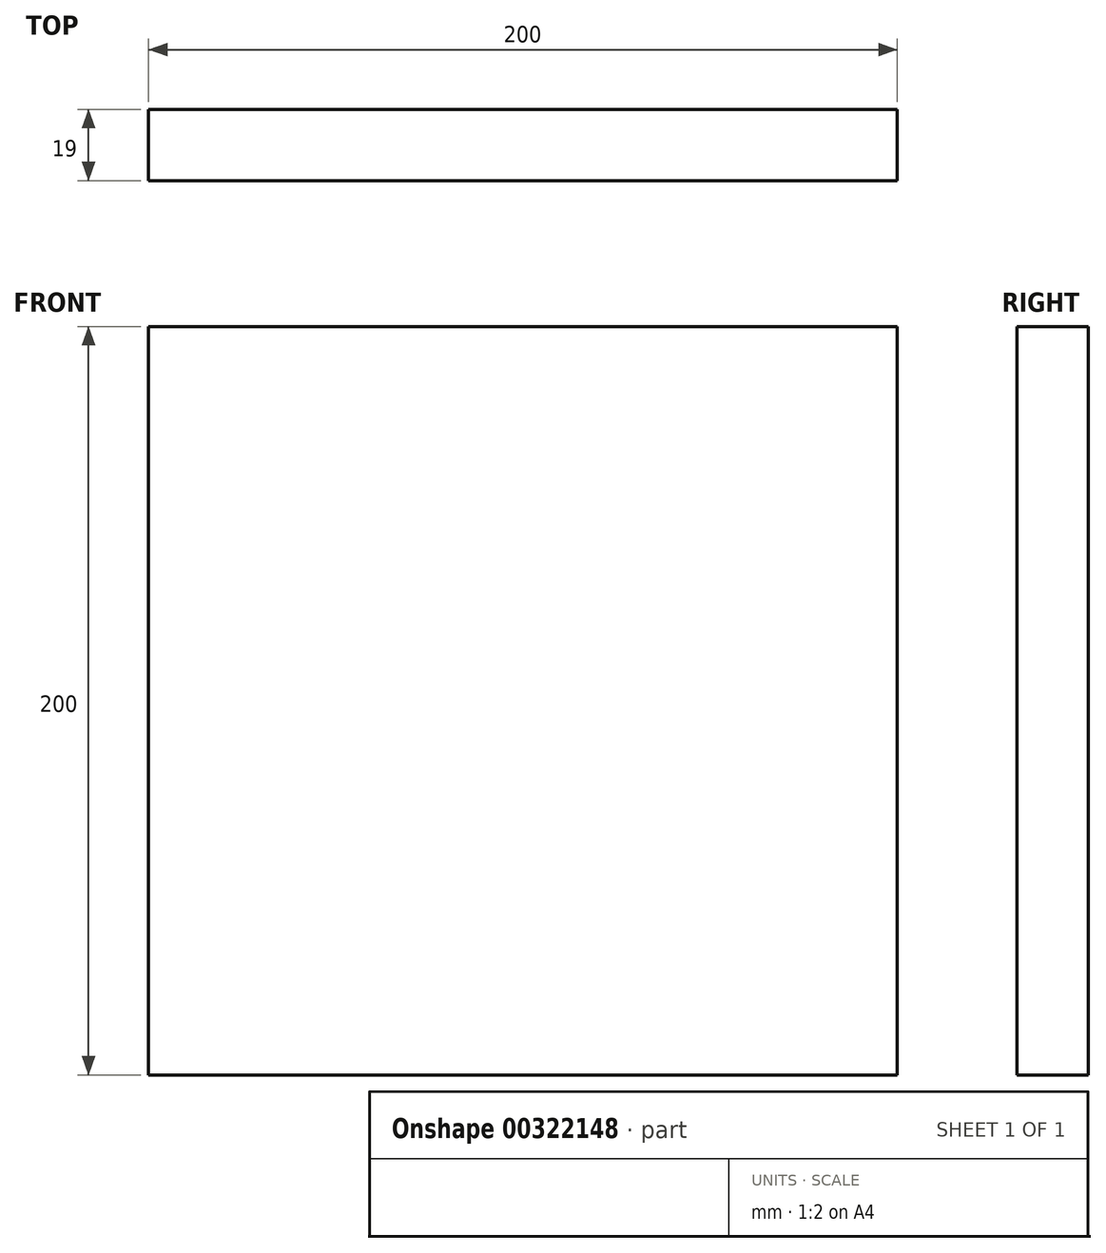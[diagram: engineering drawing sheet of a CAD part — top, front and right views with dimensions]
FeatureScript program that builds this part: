
annotation { "Feature Type Name" : "Feature", "Feature Type Description" : "" }
export const myFeature = defineFeature(function(context is Context, id is Id, definition is map)
    precondition{}
    {
        {
            var Q0;
            Q0=qCreatedBy(makeId("Front.planeOp"),FACE);
            var sketch = newSketch(context, id + "F0", { "sketchPlane" : qUnion([Q0])});
            skLineSegment(sketch, "E0.bottom", {"start": v(0, 0) * mm, "end": v(200, 0) * mm});
            skLineSegment(sketch, "E0.top", {"start": v(0, 200) * mm, "end": v(200, 200) * mm});
            skLineSegment(sketch, "E0.left", {"start": v(0, 0) * mm, "end": v(0, 200) * mm});
            skLineSegment(sketch, "E0.right", {"start": v(200, 0) * mm, "end": v(200, 200) * mm});
            skSolve(sketch);
        }
        {
            var Q0;
            Q0=makeQuery(id+"F0.imprint","IMPRINT",FACE,{"disambiguationData":[TD([[makeQuery(id+"F0.imprint","IMPRINT",EDGE,{"derivedFrom":sQuery(id+"F0.wireOp",EDGE,"E0.bottom")}),1.0]])]});
            extrude(context, id + "F1", {"entities" : qUnion([Q0]), "depth" : 19 * mm});
        }
    });
